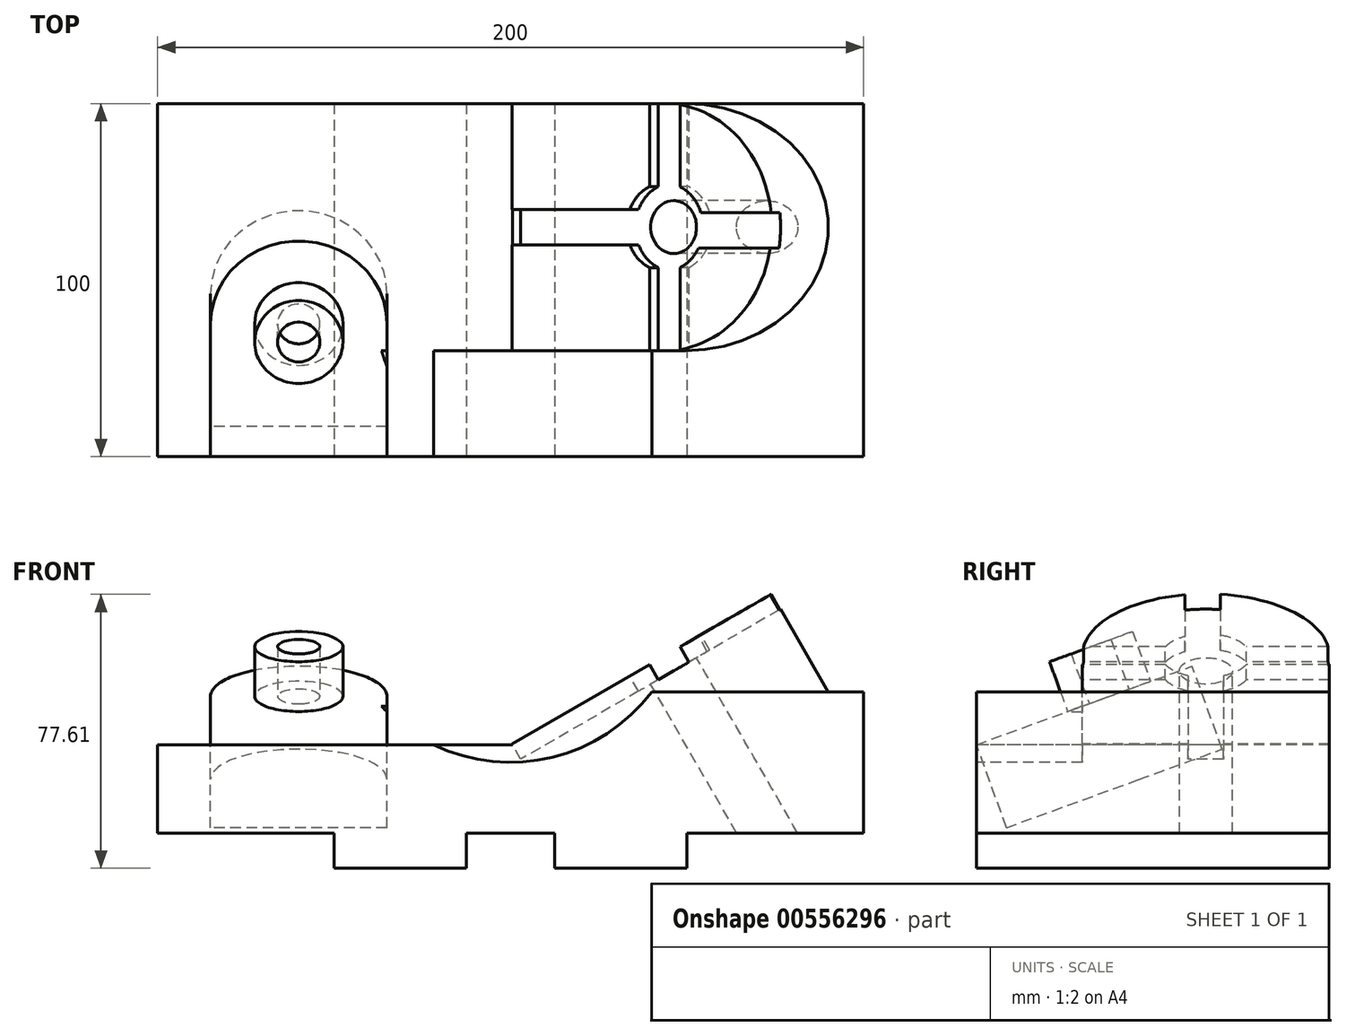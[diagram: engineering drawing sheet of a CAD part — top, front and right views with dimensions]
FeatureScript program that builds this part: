
annotation { "Feature Type Name" : "Feature", "Feature Type Description" : "" }
export const myFeature = defineFeature(function(context is Context, id is Id, definition is map)
    precondition{}
    {
        {
            var Q0;
            Q0=qCreatedBy(makeId("Front.planeOp"),FACE);
            var sketch = newSketch(context, id + "F0", { "sketchPlane" : qUnion([Q0])});
            skLineSegment(sketch, "E0.bottom", {"start": v(32.22, -3.8) * mm, "end": v(92.22, -3.8) * mm});
            skLineSegment(sketch, "E0.top", {"start": v(-57.78, -53.8) * mm, "end": v(-20.28, -53.8) * mm});
            skLineSegment(sketch, "E0.left", {"start": v(-107.78, -18.8) * mm, "end": v(-107.78, -43.8) * mm});
            skLineSegment(sketch, "E0.right", {"start": v(92.22, -3.8) * mm, "end": v(92.22, -43.8) * mm});
            skLineSegment(sketch, "E1", {"start": v(-107.78, -43.8) * mm, "end": v(-57.78, -43.8) * mm});
            skLineSegment(sketch, "E2", {"start": v(-57.78, -53.8) * mm, "end": v(-57.78, -43.8) * mm});
            skLineSegment(sketch, "E3", {"start": v(-20.28, -53.8) * mm, "end": v(-20.28, -43.8) * mm});
            skLineSegment(sketch, "E4", {"start": v(4.72, -53.8) * mm, "end": v(4.72, -43.8) * mm});
            skLineSegment(sketch, "E5", {"start": v(42.22, -53.8) * mm, "end": v(42.22, -43.8) * mm});
            skLineSegment(sketch, "E6.trimOffspring", {"start": v(4.72, -53.8) * mm, "end": v(42.22, -53.8) * mm});
            skLineSegment(sketch, "E7.trimOffspring", {"start": v(-20.28, -43.8) * mm, "end": v(4.72, -43.8) * mm});
            skLineSegment(sketch, "E8.trimOffspring", {"start": v(42.22, -43.8) * mm, "end": v(92.22, -43.8) * mm});
            skLineSegment(sketch, "E9", {"start": v(-107.78, -18.8) * mm, "end": v(32.22, -18.8) * mm});
            skLineSegment(sketch, "E10", {"start": v(32.22, -3.8) * mm, "end": v(32.22, -18.8) * mm});
            skPoint(sketch, "E11.orphan", {"position": v(92.22, -18.8) * mm});
            skSolve(sketch);
        }
        {
            var Q0;
            Q0 = qSketchRegion(id + "F0", true);
            extrude(context, id + "F1", {"entities" : qUnion([Q0]), "oppositeDirection" : true, "depth" : 100 * mm, "offsetDistance" : 25 * mm});
        }
        {
            var Q0;
            Q0=makeQuery(id+"F1.opExtrude","CAP_EDGE",EDGE,{"disambiguationData":[OSD([sQuery(id+"F0.wireOp",EDGE,"E9")])],"isStart":true});
            cPlane(context, id + "F2", {"entities" : qUnion([Q0]), "cplaneType" : CPlaneType.LINE_ANGLE, "offset" : 25 * mm, "angle" : 110 * degree, "width" : 150 * mm, "height" : 150 * mm});
        }
        {
            var Q0;
            Q0=qCreatedBy(id+"F2.planeOp",FACE);
            var sketch = newSketch(context, id + "F3", { "sketchPlane" : qUnion([Q0])});
            skLineSegment(sketch, "E12", {"start": v(-92.78, -6.43) * mm, "end": v(-92.78, 33.57) * mm});
            skLineSegment(sketch, "E13", {"start": v(-42.78, -6.43) * mm, "end": v(-42.78, 33.57) * mm});
            skLineSegment(sketch, "E14", {"start": v(-92.78, 33.57) * mm, "end": v(-42.78, 33.57) * mm, "construction": true});
            skArc(sketch, "E15", {"start": v(-42.78, 33.57) * mm, "mid": v(-67.78, 58.57) * mm, "end": v(-92.78, 33.57) * mm});
            skLineSegment(sketch, "E16", {"start": v(-42.78, -6.43) * mm, "end": v(-92.78, -6.43) * mm});
            skSolve(sketch);
        }
        {
            var Q0;
            Q0 = qSketchRegion(id + "F3", true);
            extrude(context, id + "F4", {"entities" : qUnion([Q0]), "oppositeDirection" : true, "depth" : 25 * mm, "offsetDistance" : 25 * mm});
        }
        {
            var Q0;
            Q0=makeQuery(id+"F4.opExtrude","CAP_FACE",FACE,{"disambiguationData":[OSD([sQuery(id+"F3.wireOp",EDGE,"E12"),sQuery(id+"F3.wireOp",EDGE,"E13"),sQuery(id+"F3.wireOp",EDGE,"E15"),sQuery(id+"F3.wireOp",EDGE,"E16")])],"isStart":true});
            var sketch = newSketch(context, id + "F5", { "sketchPlane" : qUnion([Q0])});
            skLineSegment(sketch, "E17", {"start": v(-92.78, 33.57) * mm, "end": v(-42.78, 33.57) * mm, "construction": true});
            skCircle(sketch, "E18", {"center": v(-67.78, 33.57) * mm, "radius": 12.5 * mm});
            skCircle(sketch, "E19", {"center": v(-67.78, 33.57) * mm, "radius": 6 * mm});
            skSolve(sketch);
        }
        {
            var Q0;
            Q0 = qSketchRegion(id + "F5", true);
            extrude(context, id + "F6", {"entities" : qUnion([Q0]), "operationType" : NewBodyOperationType.ADD, "depth" : 15 * mm, "offsetDistance" : 25 * mm});
        }
        {
            var Q0;
            Q0=makeQuery(id+"F1.opExtrude","SWEPT_FACE",FACE,{"disambiguationData":[OSD([sQuery(id+"F0.wireOp",EDGE,"E9")])]});
            var sketch = newSketch(context, id + "F7", { "sketchPlane" : qUnion([Q0])});
            skLineSegment(sketch, "E20", {"start": v(-7.78, 100) * mm, "end": v(-7.78, 0) * mm});
            skSolve(sketch);
        }
        {
            var Q0;
            Q0=sQuery(id+"F7.wireOp",EDGE,"E20");
            cPlane(context, id + "F8", {"entities" : qUnion([Q0]), "cplaneType" : CPlaneType.LINE_ANGLE, "offset" : 25 * mm, "angle" : 30 * degree, "width" : 150 * mm, "height" : 150 * mm});
        }
        {
            var Q0;
            Q0=qCreatedBy(id+"F8.planeOp",FACE);
            var sketch = newSketch(context, id + "F9", { "sketchPlane" : qUnion([Q0])});
            skLineSegment(sketch, "E21", {"start": v(-15.68, -100) * mm, "end": v(-15.68, -30) * mm});
            skLineSegment(sketch, "E22", {"start": v(-15.68, -100) * mm, "end": v(34.32, -100) * mm});
            skLineSegment(sketch, "E23", {"start": v(-15.68, -30) * mm, "end": v(34.32, -30) * mm});
            skLineSegment(sketch, "E24", {"start": v(34.32, -30) * mm, "end": v(34.32, -100) * mm, "construction": true});
            skArc(sketch, "E25", {"start": v(34.32, -100) * mm, "mid": v(69.32, -65) * mm, "end": v(34.32, -30) * mm});
            skSolve(sketch);
        }
        {
            var Q0;
            Q0 = qSketchRegion(id + "F9", true);
            var Q1;
            Q1=makeQuery(id+"F1.opExtrude","SWEPT_BODY",BODY,{"disambiguationData":[OSD([sQuery(id+"F0.wireOp",EDGE,"E0.bottom"),sQuery(id+"F0.wireOp",EDGE,"E0.top"),sQuery(id+"F0.wireOp",EDGE,"E0.left"),sQuery(id+"F0.wireOp",EDGE,"E0.right"),sQuery(id+"F0.wireOp",EDGE,"E1"),sQuery(id+"F0.wireOp",EDGE,"E2"),sQuery(id+"F0.wireOp",EDGE,"E3"),sQuery(id+"F0.wireOp",EDGE,"E4"),sQuery(id+"F0.wireOp",EDGE,"E5"),sQuery(id+"F0.wireOp",EDGE,"E6.trimOffspring"),sQuery(id+"F0.wireOp",EDGE,"E7.trimOffspring"),sQuery(id+"F0.wireOp",EDGE,"E8.trimOffspring"),sQuery(id+"F0.wireOp",EDGE,"E9"),sQuery(id+"F0.wireOp",EDGE,"E10")])]});
            extrude(context, id + "F10", {"entities" : qUnion([Q0]), "operationType" : NewBodyOperationType.ADD, "endBound" : BoundingType.UP_TO_BODY, "depth" : 25 * mm, "endBoundEntityBody" : qUnion([Q1]), "offsetDistance" : 25 * mm});
        }
        {
            var Q0;
            Q0=makeQuery(id+"F10.opExtrude","CAP_FACE",FACE,{"disambiguationData":[OSD([sQuery(id+"F9.wireOp",EDGE,"E21"),sQuery(id+"F9.wireOp",EDGE,"E22"),sQuery(id+"F9.wireOp",EDGE,"E23"),sQuery(id+"F9.wireOp",EDGE,"E25")])],"isStart":true});
            var sketch = newSketch(context, id + "F11", { "sketchPlane" : qUnion([Q0])});
            skCircle(sketch, "E26", {"center": v(34.32, 65) * mm, "radius": 7.5 * mm});
            skSolve(sketch);
        }
        {
            var Q0;
            Q0 = qSketchRegion(id + "F11", true);
            extrude(context, id + "F12", {"entities" : qUnion([Q0]), "operationType" : NewBodyOperationType.REMOVE, "endBound" : BoundingType.THROUGH_ALL, "oppositeDirection" : true, "depth" : 25 * mm, "offsetDistance" : 25 * mm});
        }
        {
            var Q0;
            Q0=makeQuery(id+"F10.opExtrude","CAP_FACE",FACE,{"disambiguationData":[OSD([sQuery(id+"F9.wireOp",EDGE,"E21"),sQuery(id+"F9.wireOp",EDGE,"E22"),sQuery(id+"F9.wireOp",EDGE,"E23"),sQuery(id+"F9.wireOp",EDGE,"E25")])],"isStart":true});
            var sketch = newSketch(context, id + "F13", { "sketchPlane" : qUnion([Q0])});
            skArc(sketch, "E27", {"start": v(39.32, 53.54) * mm, "mid": v(42.8, 55.82) * mm, "end": v(45.35, 59.1) * mm});
            skLineSegment(sketch, "E28.0", {"start": v(73, 59.1) * mm, "end": v(45.35, 59.1) * mm});
            skLineSegment(sketch, "E29.0", {"start": v(73.22, 69.1) * mm, "end": v(46.13, 69.1) * mm});
            skLineSegment(sketch, "E30.0", {"start": v(29.32, 103.01) * mm, "end": v(29.32, 76.46) * mm});
            skLineSegment(sketch, "E31.0", {"start": v(39.32, 103.01) * mm, "end": v(39.32, 76.46) * mm});
            skLineSegment(sketch, "E32.trimOffspring", {"start": v(39.32, 53.54) * mm, "end": v(39.32, 26.44) * mm});
            skLineSegment(sketch, "E33.trimOffspring", {"start": v(29.32, 53.54) * mm, "end": v(29.32, 26.44) * mm});
            skLineSegment(sketch, "E34.trimOffspring", {"start": v(22.86, 60) * mm, "end": v(-15.68, 60) * mm});
            skLineSegment(sketch, "E35.trimOffspring", {"start": v(22.86, 70) * mm, "end": v(-15.68, 70) * mm});
            skArc(sketch, "E36.trimOffspring", {"start": v(29.32, 76.46) * mm, "mid": v(25.48, 73.84) * mm, "end": v(22.86, 70) * mm});
            skArc(sketch, "E37.trimOffspring", {"start": v(46.13, 69.1) * mm, "mid": v(43.5, 73.5) * mm, "end": v(39.32, 76.46) * mm});
            skArc(sketch, "E38.trimOffspring", {"start": v(22.86, 60) * mm, "mid": v(25.48, 56.16) * mm, "end": v(29.32, 53.54) * mm});
            skLineSegment(sketch, "E39", {"start": v(-15.68, 70) * mm, "end": v(-15.68, 60) * mm});
            skLineSegment(sketch, "E40", {"start": v(73.22, 69.1) * mm, "end": v(73, 59.1) * mm});
            skLineSegment(sketch, "E41", {"start": v(39.32, 26.44) * mm, "end": v(29.32, 26.44) * mm});
            skLineSegment(sketch, "E42", {"start": v(39.32, 103.01) * mm, "end": v(29.32, 103.01) * mm});
            skSolve(sketch);
        }
        {
            var Q0;
            Q0 = qSketchRegion(id + "F13", true);
            extrude(context, id + "F14", {"entities" : qUnion([Q0]), "operationType" : NewBodyOperationType.REMOVE, "oppositeDirection" : true, "depth" : 5 * mm, "offsetDistance" : 25 * mm});
        }
        {
            var Q0;
            Q0=makeQuery(id+"F1.opExtrude","SWEPT_FACE",FACE,{"disambiguationData":[OSD([sQuery(id+"F0.wireOp",EDGE,"E10")])]});
            var sketch = newSketch(context, id + "F15", { "sketchPlane" : qUnion([Q0])});
            skLineSegment(sketch, "E43", {"start": v(-30, -3.8) * mm, "end": v(0, -3.8) * mm});
            skLineSegment(sketch, "E44", {"start": v(0, -3.8) * mm, "end": v(0, -18.8) * mm});
            skLineSegment(sketch, "E45", {"start": v(0, -18.8) * mm, "end": v(-30, -18.8) * mm});
            skLineSegment(sketch, "E46", {"start": v(-30, -18.8) * mm, "end": v(-30, -3.8) * mm});
            skSolve(sketch);
        }
        {
            var Q0;
            Q0 = qSketchRegion(id + "F15", true);
            extrude(context, id + "F16", {"entities" : qUnion([Q0]), "operationType" : NewBodyOperationType.ADD, "depth" : 25 * mm, "offsetDistance" : 25 * mm});
        }
        {
            var Q0;
            Q0=makeQuery(id+"F1.opExtrude","CAP_FACE",FACE,{"disambiguationData":[OSD([sQuery(id+"F0.wireOp",EDGE,"E0.bottom"),sQuery(id+"F0.wireOp",EDGE,"E0.top"),sQuery(id+"F0.wireOp",EDGE,"E0.left"),sQuery(id+"F0.wireOp",EDGE,"E0.right"),sQuery(id+"F0.wireOp",EDGE,"E1"),sQuery(id+"F0.wireOp",EDGE,"E2"),sQuery(id+"F0.wireOp",EDGE,"E3"),sQuery(id+"F0.wireOp",EDGE,"E4"),sQuery(id+"F0.wireOp",EDGE,"E5"),sQuery(id+"F0.wireOp",EDGE,"E6.trimOffspring"),sQuery(id+"F0.wireOp",EDGE,"E7.trimOffspring"),sQuery(id+"F0.wireOp",EDGE,"E8.trimOffspring"),sQuery(id+"F0.wireOp",EDGE,"E9"),sQuery(id+"F0.wireOp",EDGE,"E10")])],"isStart":true});
            var sketch = newSketch(context, id + "F17", { "sketchPlane" : qUnion([Q0])});
            skLineSegment(sketch, "E47", {"start": v(-7.78, -23.8) * mm, "end": v(-7.78, 26.2) * mm, "construction": true});
            skCircle(sketch, "E48", {"center": v(-7.78, 26.2) * mm, "radius": 50 * mm});
            skSolve(sketch);
        }
        {
            var Q0;
            Q0 = qSketchRegion(id + "F17", true);
            var Q1;
            {var subQ1=sQuery(id+"F9.wireOp",EDGE,"E23");Q1=makeQuery(id+"F16.boolean.opBoolean","SPLIT",FACE,{"disambiguationData":[TD([makeQuery(id+"F1.opExtrude","SWEPT_FACE",FACE,{"disambiguationData":[OSD([sQuery(id+"F0.wireOp",EDGE,"E9")])]})])],"derivedFrom":makeQuery(id+"F10.opExtrude","SWEPT_FACE",FACE,{"disambiguationData":[OSD([subQ1])]})});}
            extrude(context, id + "F18", {"entities" : qUnion([Q0]), "operationType" : NewBodyOperationType.REMOVE, "endBound" : BoundingType.UP_TO_SURFACE, "oppositeDirection" : true, "depth" : 25 * mm, "endBoundEntityFace" : qUnion([Q1]), "offsetDistance" : 25 * mm});
        }
    });
